# Revit family: LC5
name_source: partatom
category: Lighting Fixtures
units: mm (PartAtom-declared; Revit-internal decimal feet)

## family parameters
Cut with Voids When Loaded = No
Host = Face
Light Source = Yes
OmniClass Number = 23.80.70.14
OmniClass Title = Luminaries for External Lighting
Part Type = Normal
Room Calculation Point = No
Round Connector Dimension = Use Diameter
Shared = No

## types (12) — shared parameters
Apparent Load = 0 VA
Color Filter = 16777215
Default Elevation = 4' - 0"
Description = The LC5 column light offers the sophistication required to enhance any public space, and utilizes the energy efficiency of an LED light engine and tube technology.
Dimming Lamp Color Temperature Shift = <None>
Emit from Line Length = 2' - 0"
Height = 6' - 0"
Lens Finish = Glass
Manufacturer = Beacon Products
Model = LC5
Photometric Web File = generic
Tilt Angle = 90.00°
URL = https://www.currentlighting.com
Voltage = 120 V
Wattage Comments = 55W

## per-type parameters (varying)
| type | Product Material |
| Basic Black Textured | Paint -  Basic Black Textured |
| Black Matte Textured | Paint - Black Matte Textured |
| Bronze Textured | Paint - Bronze Textured |
| Dark Bronze Textured | Paint - Dark Bronze Textured |
| Dark Platinum Smooth | Paint - Dark Platinum Smooth |
| Gray Smooth | Paint -  Gray Smooth |
| Green Textured | Paint - Green Textured |
| Metallic Bronze Textured | Paint - Metallic Bronze Textured |
| Metallic Silver Textured | Paint -  Metallic Silver Textured |
| Metallic Titanium Textured | Paint -  Metallic Titanium Textured |
| Old World Iron | Paint - Old World Iron |
| White Texture | Paint -  White Texture |

## geometry (parser evidence)
native form markers: Sweep x3
no freeform markers — native parametric forms only
